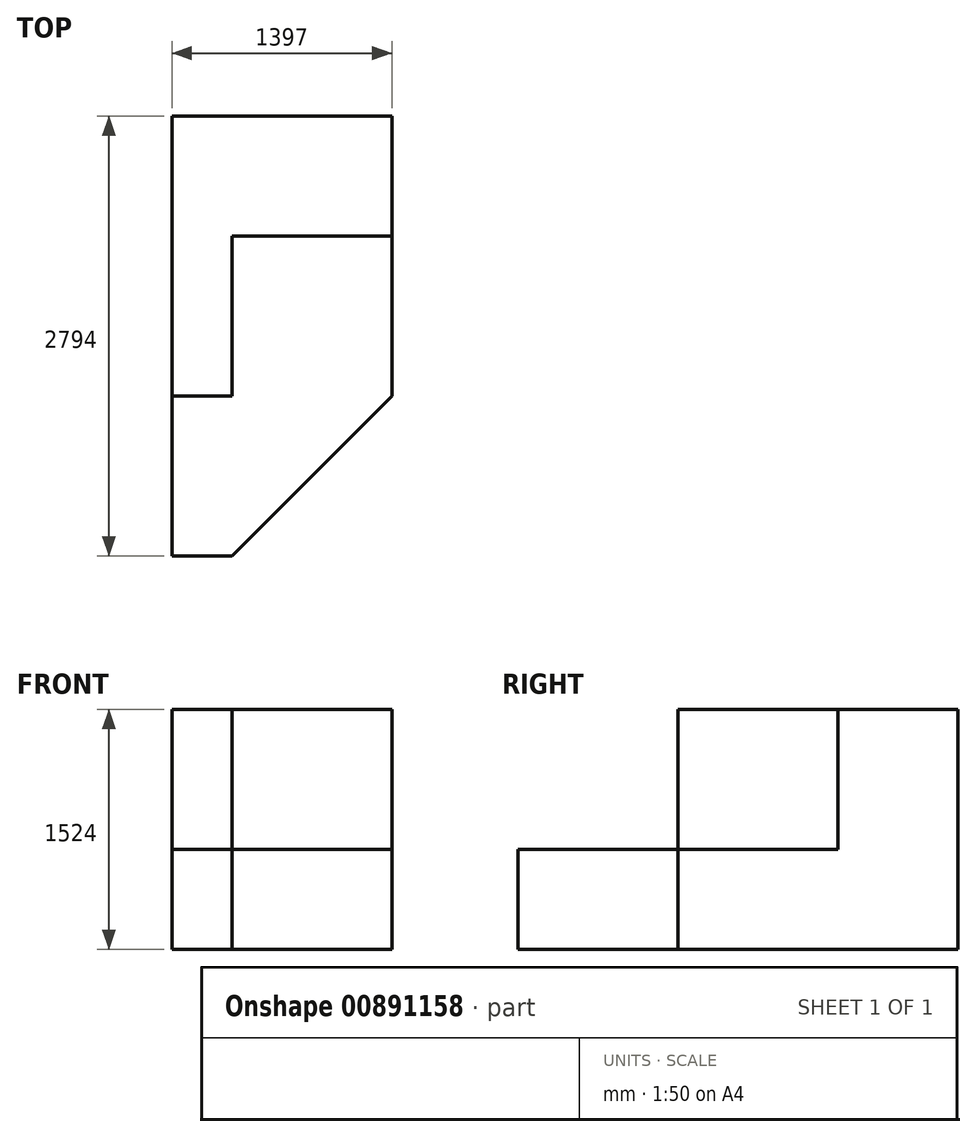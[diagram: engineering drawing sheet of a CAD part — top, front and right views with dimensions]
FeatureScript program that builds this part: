
annotation { "Feature Type Name" : "Feature", "Feature Type Description" : "" }
export const myFeature = defineFeature(function(context is Context, id is Id, definition is map)
    precondition{}
    {
        {
            var Q0;
            Q0=qCreatedBy(makeId("Top.planeOp"),FACE);
            var sketch = newSketch(context, id + "F0", { "sketchPlane" : qUnion([Q0])});
            skLineSegment(sketch, "E0.bottom", {"start": v(0, 0) * mm, "end": v(-1397, 0) * mm});
            skLineSegment(sketch, "E0.top", {"start": v(0, -2794) * mm, "end": v(-1397, -2794) * mm});
            skLineSegment(sketch, "E0.left", {"start": v(0, 0) * mm, "end": v(0, -2794) * mm});
            skLineSegment(sketch, "E0.right", {"start": v(-1397, 0) * mm, "end": v(-1397, -2794) * mm});
            skSolve(sketch);
        }
        {
            var Q0;
            Q0=makeQuery(id+"F0.imprint","IMPRINT",FACE,{"disambiguationData":[TD([[makeQuery(id+"F0.imprint","IMPRINT",EDGE,{"derivedFrom":sQuery(id+"F0.wireOp",EDGE,"E0.bottom")}),1.0]])]});
            extrude(context, id + "F1", {"entities" : qUnion([Q0]), "depth" : 1524 * mm, "offsetDistance" : 25.4 * mm});
        }
        {
            var Q0;
            Q0=makeQuery(id+"F1.opExtrude","CAP_FACE",FACE,{"disambiguationData":[OSD([sQuery(id+"F0.wireOp",EDGE,"E0.bottom"),sQuery(id+"F0.wireOp",EDGE,"E0.top"),sQuery(id+"F0.wireOp",EDGE,"E0.left"),sQuery(id+"F0.wireOp",EDGE,"E0.right")])],"isStart":false});
            var sketch = newSketch(context, id + "F2", { "sketchPlane" : qUnion([Q0])});
            skLineSegment(sketch, "E1", {"start": v(-1397, 0) * mm, "end": v(-1397, -1778) * mm});
            skLineSegment(sketch, "E2", {"start": v(-1397, -1778) * mm, "end": v(-1016, -1778) * mm});
            skLineSegment(sketch, "E3", {"start": v(-1016, -1778) * mm, "end": v(-1016, -762) * mm});
            skLineSegment(sketch, "E4", {"start": v(-1016, -762) * mm, "end": v(0, -762) * mm});
            skSolve(sketch);
        }
        {
            var Q0;
            {var subQ2=sQuery(id+"F2.wireOp",EDGE,"E2");Q0=makeQuery(id+"F2.imprint","IMPRINT",FACE,{"disambiguationData":[TD([[makeQuery(id+"F2.imprint","IMPRINT",EDGE,{"derivedFrom":subQ2}),-1.0]])]});}
            extrude(context, id + "F3", {"entities" : qUnion([Q0]), "operationType" : NewBodyOperationType.REMOVE, "oppositeDirection" : true, "depth" : 889 * mm, "offsetDistance" : 25.4 * mm});
        }
        {
            var Q0;
            Q0=makeQuery(id+"F3.boolean.opBoolean","COPY",FACE,{"derivedFrom":makeQuery(id+"F3.opExtrude","CAP_FACE",FACE,{"disambiguationData":[OSD([sQuery(id+"F0.wireOp",EDGE,"E0.top"),sQuery(id+"F0.wireOp",EDGE,"E0.left"),sQuery(id+"F0.wireOp",EDGE,"E0.right"),sQuery(id+"F2.wireOp",EDGE,"E2"),sQuery(id+"F2.wireOp",EDGE,"E3"),sQuery(id+"F2.wireOp",EDGE,"E4")])],"isStart":false})});
            var sketch = newSketch(context, id + "F4", { "sketchPlane" : qUnion([Q0])});
            skLineSegment(sketch, "E5", {"start": v(0, -762) * mm, "end": v(0, -1778) * mm});
            skLineSegment(sketch, "E6", {"start": v(0, -1778) * mm, "end": v(-1016, -2794) * mm});
            skSolve(sketch);
        }
        {
            var Q0;
            {var subQ0=sQuery(id+"F4.wireOp",EDGE,"E6");Q0=makeQuery(id+"F4.imprint","IMPRINT",FACE,{"disambiguationData":[TD([[makeQuery(id+"F4.imprint","IMPRINT",EDGE,{"derivedFrom":subQ0}),1.0]])]});}
            extrude(context, id + "F5", {"entities" : qUnion([Q0]), "operationType" : NewBodyOperationType.REMOVE, "oppositeDirection" : true, "depth" : 932.18 * mm, "offsetDistance" : 25.4 * mm});
        }
    });
